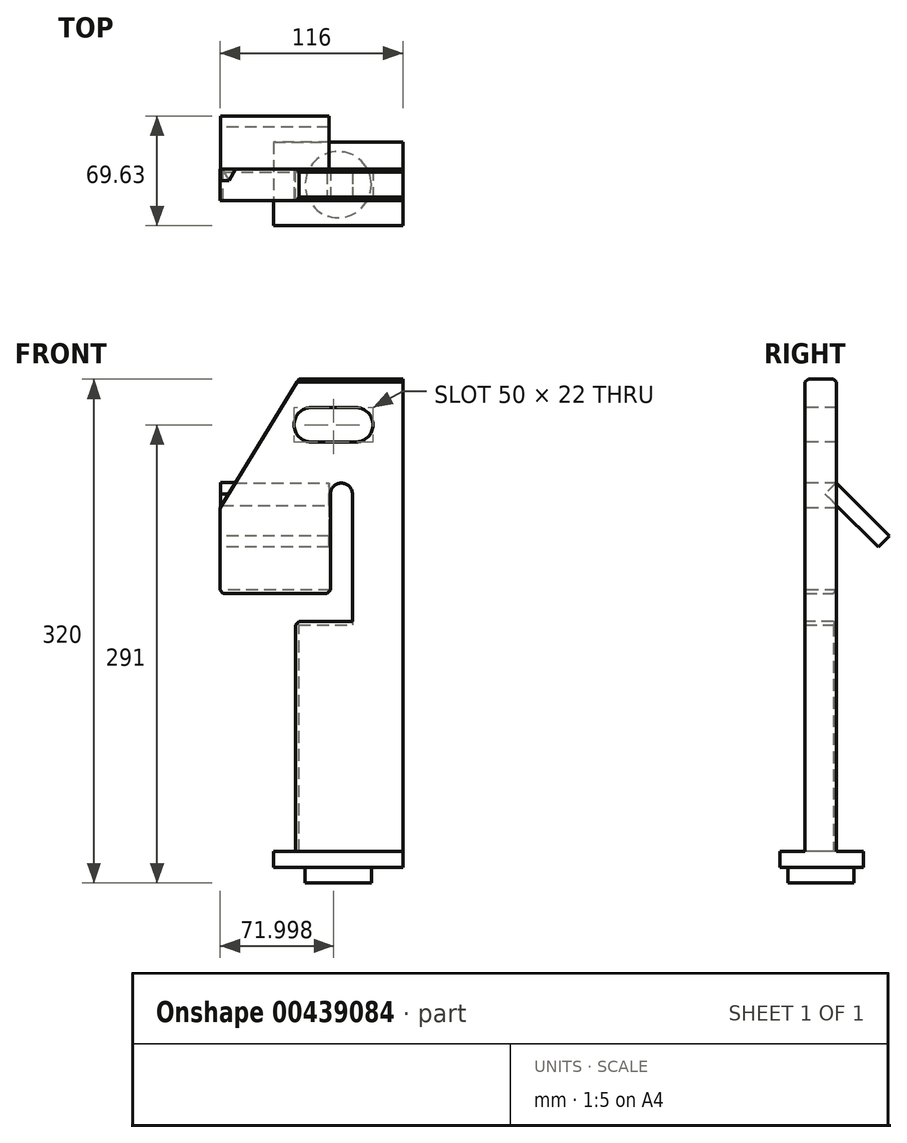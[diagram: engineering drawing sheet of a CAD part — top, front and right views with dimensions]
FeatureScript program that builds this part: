
annotation { "Feature Type Name" : "Feature", "Feature Type Description" : "" }
export const myFeature = defineFeature(function(context is Context, id is Id, definition is map)
    precondition{}
    {
        {
            var Q0;
            Q0=qCreatedBy(makeId("Front.planeOp"),FACE);
            var sketch = newSketch(context, id + "F0", { "sketchPlane" : qUnion([Q0])});
            skLineSegment(sketch, "E0.bottom", {"start": v(-146.6, 260.99) * mm, "end": v(-30.6, 260.99) * mm});
            skLineSegment(sketch, "E0.top", {"start": v(-146.6, -39.01) * mm, "end": v(-30.6, -39.01) * mm});
            skLineSegment(sketch, "E0.left", {"start": v(-146.6, 260.99) * mm, "end": v(-146.6, -39.01) * mm});
            skLineSegment(sketch, "E0.right", {"start": v(-30.6, 260.99) * mm, "end": v(-30.6, -39.01) * mm});
            skLineSegment(sketch, "E1.bottom", {"start": v(-30.6, -39.01) * mm, "end": v(-112.6, -39.01) * mm});
            skLineSegment(sketch, "E1.top", {"start": v(-30.6, -49.01) * mm, "end": v(-112.6, -49.01) * mm});
            skLineSegment(sketch, "E1.left", {"start": v(-30.6, -39.01) * mm, "end": v(-30.6, -49.01) * mm});
            skLineSegment(sketch, "E1.right", {"start": v(-112.6, -39.01) * mm, "end": v(-112.6, -49.01) * mm});
            skLineSegment(sketch, "E2.top", {"start": v(-50.6, -49.01) * mm, "end": v(-92.6, -49.01) * mm});
            skSolve(sketch);
        }
        {
            var Q0;
            Q0 = qSketchRegion(id + "F0", true);
            extrude(context, id + "F1", {"entities" : qUnion([Q0]), "oppositeDirection" : true, "depth" : 20 * mm, "offsetDistance" : 25 * mm});
        }
        {
            var Q0;
            Q0=makeQuery(id+"F1.opExtrude","CAP_FACE",FACE,{"disambiguationData":[OSD([sQuery(id+"F0.wireOp",EDGE,"E0.bottom"),sQuery(id+"F0.wireOp",EDGE,"E0.top"),sQuery(id+"F0.wireOp",EDGE,"E0.left"),sQuery(id+"F0.wireOp",EDGE,"E0.right")])],"isStart":true});
            var sketch = newSketch(context, id + "F2", { "sketchPlane" : qUnion([Q0])});
            skLineSegment(sketch, "E3.bottom", {"start": v(-158.6, -39.01) * mm, "end": v(-98.6, -39.01) * mm});
            skLineSegment(sketch, "E3.top", {"start": v(-158.6, 124.99) * mm, "end": v(-98.6, 124.99) * mm});
            skLineSegment(sketch, "E3.left", {"start": v(-158.6, -39.01) * mm, "end": v(-158.6, 124.99) * mm});
            skLineSegment(sketch, "E3.right", {"start": v(-98.6, -39.01) * mm, "end": v(-98.6, 124.99) * mm});
            skLineSegment(sketch, "E4.bottom", {"start": v(-98.6, 124.99) * mm, "end": v(-62.6, 124.99) * mm});
            skLineSegment(sketch, "E4.top", {"start": v(-98.6, 106.99) * mm, "end": v(-62.6, 106.99) * mm});
            skLineSegment(sketch, "E4.left", {"start": v(-98.6, 124.99) * mm, "end": v(-98.6, 106.99) * mm});
            skLineSegment(sketch, "E4.right", {"start": v(-62.6, 124.99) * mm, "end": v(-62.6, 106.99) * mm});
            skLineSegment(sketch, "E5.bottom", {"start": v(-62.6, 124.99) * mm, "end": v(-76.6, 124.99) * mm});
            skLineSegment(sketch, "E5.top", {"start": v(-62.6, 187.99) * mm, "end": v(-76.6, 187.99) * mm});
            skLineSegment(sketch, "E5.left", {"start": v(-62.6, 124.99) * mm, "end": v(-62.6, 187.99) * mm});
            skLineSegment(sketch, "E5.right", {"start": v(-76.6, 124.99) * mm, "end": v(-76.6, 187.99) * mm});
            skArc(sketch, "E6", {"start": v(-62.6, 187.99) * mm, "mid": v(-69.6, 194.99) * mm, "end": v(-76.6, 187.99) * mm});
            skLineSegment(sketch, "E7", {"start": v(-96.6, 260.99) * mm, "end": v(-146.6, 178.99) * mm});
            skSolve(sketch);
        }
        {
            var Q0;
            Q0 = qSketchRegion(id + "F2", true);
            var Q1;
            {var subQ0=sQuery(id+"F2.wireOp",EDGE,"E7");Q1=makeQuery(id+"F2.imprint","IMPRINT",FACE,{"disambiguationData":[TD([[makeQuery(id+"F2.imprint","IMPRINT",EDGE,{"derivedFrom":subQ0}),-1.0]])]});}
            extrude(context, id + "F3", {"entities" : qUnion([Q0, Q1]), "operationType" : NewBodyOperationType.REMOVE, "oppositeDirection" : true, "depth" : 25 * mm, "offsetDistance" : 25 * mm});
        }
        {
            var Q0;
            Q0=makeQuery(id+"F1.opExtrude","CAP_FACE",FACE,{"disambiguationData":[OSD([sQuery(id+"F0.wireOp",EDGE,"E0.bottom"),sQuery(id+"F0.wireOp",EDGE,"E0.top"),sQuery(id+"F0.wireOp",EDGE,"E0.left"),sQuery(id+"F0.wireOp",EDGE,"E0.right")])],"isStart":true});
            var sketch = newSketch(context, id + "F4", { "sketchPlane" : qUnion([Q0])});
            skLineSegment(sketch, "E8.bottom", {"start": v(-60.6, 242.99) * mm, "end": v(-88.6, 242.99) * mm});
            skLineSegment(sketch, "E8.top", {"start": v(-60.6, 220.99) * mm, "end": v(-88.6, 220.99) * mm});
            skLineSegment(sketch, "E8.left", {"start": v(-60.6, 242.99) * mm, "end": v(-60.6, 220.99) * mm});
            skLineSegment(sketch, "E8.right", {"start": v(-88.6, 242.99) * mm, "end": v(-88.6, 220.99) * mm});
            skArc(sketch, "E9", {"start": v(-60.6, 220.99) * mm, "mid": v(-49.6, 231.99) * mm, "end": v(-60.6, 242.99) * mm});
            skArc(sketch, "E10", {"start": v(-88.6, 242.99) * mm, "mid": v(-99.6, 231.99) * mm, "end": v(-88.6, 220.99) * mm});
            skSolve(sketch);
        }
        {
            var Q0;
            Q0 = qSketchRegion(id + "F4", true);
            extrude(context, id + "F5", {"entities" : qUnion([Q0]), "operationType" : NewBodyOperationType.REMOVE, "oppositeDirection" : true, "depth" : 25 * mm, "offsetDistance" : 25 * mm});
        }
        {
            var Q0;
            Q0=makeQuery(id+"F1.opExtrude","CAP_FACE",FACE,{"disambiguationData":[OSD([sQuery(id+"F0.wireOp",EDGE,"E0.bottom"),sQuery(id+"F0.wireOp",EDGE,"E0.top"),sQuery(id+"F0.wireOp",EDGE,"E0.left"),sQuery(id+"F0.wireOp",EDGE,"E0.right"),sQuery(id+"F0.wireOp",EDGE,"E1.top"),sQuery(id+"F0.wireOp",EDGE,"E1.left"),sQuery(id+"F0.wireOp",EDGE,"E1.right"),sQuery(id+"F0.wireOp",EDGE,"E2.bottom"),sQuery(id+"F0.wireOp",EDGE,"E2.left"),sQuery(id+"F0.wireOp",EDGE,"E2.right")])],"isStart":true});
            var sketch = newSketch(context, id + "F6", { "sketchPlane" : qUnion([Q0])});
            skLineSegment(sketch, "E11", {"start": v(-98.6, -39.01) * mm, "end": v(-30.6, -39.01) * mm});
            skLineSegment(sketch, "E12", {"start": v(-30.6, -49.01) * mm, "end": v(-30.6, -49.01) * mm});
            skSolve(sketch);
        }
        {
            var Q0;
            {var subQ6=sQuery(id+"F6.wireOp",EDGE,"E11");Q0=makeQuery(id+"F6.imprint","IMPRINT",FACE,{"disambiguationData":[TD([[makeQuery(id+"F6.imprint","IMPRINT",EDGE,{"derivedFrom":subQ6}),-1.0]])]});}
            extrude(context, id + "F7", {"entities" : qUnion([Q0]), "operationType" : NewBodyOperationType.ADD, "depth" : 16 * mm, "offsetDistance" : 25 * mm});
        }
        {
            var Q0;
            Q0=makeQuery(id+"F1.opExtrude","CAP_FACE",FACE,{"disambiguationData":[OSD([sQuery(id+"F0.wireOp",EDGE,"E0.bottom"),sQuery(id+"F0.wireOp",EDGE,"E0.top"),sQuery(id+"F0.wireOp",EDGE,"E0.left"),sQuery(id+"F0.wireOp",EDGE,"E0.right"),sQuery(id+"F0.wireOp",EDGE,"E1.top"),sQuery(id+"F0.wireOp",EDGE,"E1.left"),sQuery(id+"F0.wireOp",EDGE,"E1.right"),sQuery(id+"F0.wireOp",EDGE,"E2.bottom"),sQuery(id+"F0.wireOp",EDGE,"E2.left"),sQuery(id+"F0.wireOp",EDGE,"E2.right")])],"isStart":false});
            var sketch = newSketch(context, id + "F8", { "sketchPlane" : qUnion([Q0])});
            skLineSegment(sketch, "E13", {"start": v(98.6, -39.01) * mm, "end": v(30.6, -39.01) * mm});
            skLineSegment(sketch, "E14", {"start": v(30.6, -49.01) * mm, "end": v(30.6, -49.01) * mm});
            skSolve(sketch);
        }
        {
            var Q0;
            {var subQ0=sQuery(id+"F0.wireOp",EDGE,"E2.top");var subQ1=sQuery(id+"F0.wireOp",EDGE,"E1.top");Q0=makeQuery(id+"F10.boolean.opBoolean","MERGE",FACE,{"derivedFrom":[makeQuery(id+"F7.boolean.opBoolean","MERGE",FACE,{"derivedFrom":[makeQuery(id+"F1.opExtrude","SWEPT_FACE",FACE,{"disambiguationData":[OSD([subQ1,subQ0])]}),makeQuery(id+"F7.opExtrude","SWEPT_FACE",FACE,{"disambiguationData":[OSD([subQ1,subQ0])]})]}),makeQuery(id+"F10.opExtrude","SWEPT_FACE",FACE,{"disambiguationData":[OSD([subQ1,subQ0])]})]});}
            var sketch = newSketch(context, id + "F9", { "sketchPlane" : qUnion([Q0])});
            skCircle(sketch, "E15", {"center": v(-71.6, -10) * mm, "radius": 21 * mm});
            skSolve(sketch);
        }
        {
            var Q0;
            {var subQ9=sQuery(id+"F8.wireOp",EDGE,"E13");Q0=makeQuery(id+"F8.imprint","IMPRINT",FACE,{"disambiguationData":[TD([[makeQuery(id+"F8.imprint","IMPRINT",EDGE,{"derivedFrom":subQ9}),1.0]])]});}
            extrude(context, id + "F10", {"entities" : qUnion([Q0]), "operationType" : NewBodyOperationType.ADD, "depth" : 17 * mm, "offsetDistance" : 25 * mm});
        }
        {
            var Q0;
            Q0 = qSketchRegion(id + "F9", true);
            extrude(context, id + "F11", {"entities" : qUnion([Q0]), "operationType" : NewBodyOperationType.ADD, "depth" : 10 * mm, "offsetDistance" : 25 * mm});
        }
        {
            var Q0;
            Q0=makeQuery(id+"F1.opExtrude","CAP_FACE",FACE,{"disambiguationData":[OSD([sQuery(id+"F0.wireOp",EDGE,"E0.bottom"),sQuery(id+"F0.wireOp",EDGE,"E0.top"),sQuery(id+"F0.wireOp",EDGE,"E0.left"),sQuery(id+"F0.wireOp",EDGE,"E0.right"),sQuery(id+"F0.wireOp",EDGE,"E1.top"),sQuery(id+"F0.wireOp",EDGE,"E1.left"),sQuery(id+"F0.wireOp",EDGE,"E1.right"),sQuery(id+"F0.wireOp",EDGE,"E2.top")])],"isStart":false});
            var sketch = newSketch(context, id + "F12", { "sketchPlane" : qUnion([Q0])});
            skLineSegment(sketch, "E16", {"start": v(69.6, 194.99) * mm, "end": v(136.84, 194.99) * mm});
            skSolve(sketch);
        }
        {
            var Q0;
            Q0=makeQuery(id+"F3.boolean.opBoolean","COPY",EDGE,{"derivedFrom":makeQuery(id+"F3.opExtrude","CAP_EDGE",EDGE,{"disambiguationData":[OSD([sQuery(id+"F2.wireOp",EDGE,"E3.right")])],"isStart":true})});
            var Q1;
            Q1=makeQuery(id+"F3.boolean.opBoolean","INTERSECT",EDGE,{"derivedFrom":[makeQuery(id+"F1.opExtrude","CAP_FACE",FACE,{"disambiguationData":[OSD([sQuery(id+"F0.wireOp",EDGE,"E0.bottom"),sQuery(id+"F0.wireOp",EDGE,"E0.top"),sQuery(id+"F0.wireOp",EDGE,"E0.left"),sQuery(id+"F0.wireOp",EDGE,"E0.right"),sQuery(id+"F0.wireOp",EDGE,"E1.top"),sQuery(id+"F0.wireOp",EDGE,"E1.left"),sQuery(id+"F0.wireOp",EDGE,"E1.right"),sQuery(id+"F0.wireOp",EDGE,"E2.bottom"),sQuery(id+"F0.wireOp",EDGE,"E2.left"),sQuery(id+"F0.wireOp",EDGE,"E2.right")])],"isStart":false}),makeQuery(id+"F3.opExtrude","SWEPT_FACE",FACE,{"disambiguationData":[OSD([sQuery(id+"F2.wireOp",EDGE,"E3.right")])]})]});
            chamfer(context, id + "F13", {"entities" : qUnion([Q0, Q1]), "width" : 2 * mm, "tangentPropagation" : true});
        }
        {
            var Q0;
            Q0=makeQuery(id+"F3.boolean.opBoolean","INTERSECT",EDGE,{"derivedFrom":[makeQuery(id+"F1.opExtrude","SWEPT_FACE",FACE,{"disambiguationData":[OSD([sQuery(id+"F0.wireOp",EDGE,"E0.left")])]}),makeQuery(id+"F3.opExtrude","SWEPT_FACE",FACE,{"disambiguationData":[OSD([sQuery(id+"F2.wireOp",EDGE,"E3.top"),sQuery(id+"F2.wireOp",EDGE,"E4.bottom")])]})]});
            var Q1;
            Q1=makeQuery(id+"F3.boolean.opBoolean","COPY",EDGE,{"derivedFrom":makeQuery(id+"F3.opExtrude","SWEPT_EDGE",EDGE,{"disambiguationData":[OSD([sQuery(id+"F2.wireOp",EDGE,"E3.right"),sQuery(id+"F2.wireOp",EDGE,"E4.top"),sQuery(id+"F2.wireOp",EDGE,"E4.left")])]})});
            var Q2;
            Q2=makeQuery(id+"F3.boolean.opBoolean","COPY",EDGE,{"derivedFrom":makeQuery(id+"F3.opExtrude","SWEPT_EDGE",EDGE,{"disambiguationData":[OSD([sQuery(id+"F2.wireOp",EDGE,"E4.bottom"),sQuery(id+"F2.wireOp",EDGE,"E5.bottom"),sQuery(id+"F2.wireOp",EDGE,"E5.right")])]})});
            var Q3;
            Q3=makeQuery(id+"F3.boolean.opBoolean","COPY",EDGE,{"derivedFrom":makeQuery(id+"F3.opExtrude","SWEPT_EDGE",EDGE,{"disambiguationData":[OSD([sQuery(id+"F0.wireOp",EDGE,"E0.bottom"),sQuery(id+"F2.wireOp",EDGE,"E7")])]})});
            chamfer(context, id + "F14", {"entities" : qUnion([Q0, Q1, Q2, Q3]), "width" : 2 * mm, "tangentPropagation" : true});
        }
        {
            var Q0;
            Q0=makeQuery(id+"F3.boolean.opBoolean","COPY",EDGE,{"derivedFrom":makeQuery(id+"F3.opExtrude","CAP_EDGE",EDGE,{"disambiguationData":[OSD([sQuery(id+"F2.wireOp",EDGE,"E3.top"),sQuery(id+"F2.wireOp",EDGE,"E4.bottom")])],"isStart":true})});
            var Q1;
            Q1=makeQuery(id+"F3.boolean.opBoolean","INTERSECT",EDGE,{"derivedFrom":[makeQuery(id+"F1.opExtrude","CAP_FACE",FACE,{"disambiguationData":[OSD([sQuery(id+"F0.wireOp",EDGE,"E0.bottom"),sQuery(id+"F0.wireOp",EDGE,"E0.top"),sQuery(id+"F0.wireOp",EDGE,"E0.left"),sQuery(id+"F0.wireOp",EDGE,"E0.right"),sQuery(id+"F0.wireOp",EDGE,"E1.top"),sQuery(id+"F0.wireOp",EDGE,"E1.left"),sQuery(id+"F0.wireOp",EDGE,"E1.right"),sQuery(id+"F0.wireOp",EDGE,"E2.bottom"),sQuery(id+"F0.wireOp",EDGE,"E2.left"),sQuery(id+"F0.wireOp",EDGE,"E2.right")])],"isStart":false}),makeQuery(id+"F3.opExtrude","SWEPT_FACE",FACE,{"disambiguationData":[OSD([sQuery(id+"F2.wireOp",EDGE,"E3.top"),sQuery(id+"F2.wireOp",EDGE,"E4.bottom")])]})]});
            var Q2;
            Q2=makeQuery(id+"F3.boolean.opBoolean","COPY",EDGE,{"derivedFrom":makeQuery(id+"F3.opExtrude","CAP_EDGE",EDGE,{"disambiguationData":[OSD([sQuery(id+"F2.wireOp",EDGE,"E4.top")])],"isStart":true})});
            var Q3;
            Q3=makeQuery(id+"F3.boolean.opBoolean","INTERSECT",EDGE,{"derivedFrom":[makeQuery(id+"F1.opExtrude","CAP_FACE",FACE,{"disambiguationData":[OSD([sQuery(id+"F0.wireOp",EDGE,"E0.bottom"),sQuery(id+"F0.wireOp",EDGE,"E0.top"),sQuery(id+"F0.wireOp",EDGE,"E0.left"),sQuery(id+"F0.wireOp",EDGE,"E0.right"),sQuery(id+"F0.wireOp",EDGE,"E1.top"),sQuery(id+"F0.wireOp",EDGE,"E1.left"),sQuery(id+"F0.wireOp",EDGE,"E1.right"),sQuery(id+"F0.wireOp",EDGE,"E2.bottom"),sQuery(id+"F0.wireOp",EDGE,"E2.left"),sQuery(id+"F0.wireOp",EDGE,"E2.right")])],"isStart":false}),makeQuery(id+"F3.opExtrude","SWEPT_FACE",FACE,{"disambiguationData":[OSD([sQuery(id+"F2.wireOp",EDGE,"E4.top")])]})]});
            var Q4;
            Q4=makeQuery(id+"F1.opExtrude","CAP_EDGE",EDGE,{"disambiguationData":[OSD([sQuery(id+"F0.wireOp",EDGE,"E0.bottom")])],"isStart":true});
            var Q5;
            Q5=makeQuery(id+"F1.opExtrude","CAP_EDGE",EDGE,{"disambiguationData":[OSD([sQuery(id+"F0.wireOp",EDGE,"E0.bottom")])],"isStart":false});
            chamfer(context, id + "F15", {"entities" : qUnion([Q0, Q1, Q2, Q3, Q4, Q5]), "width" : 2 * mm, "tangentPropagation" : true});
        }
        {
            var Q0;
            Q0=makeQuery(id+"F1.opExtrude","CAP_FACE",FACE,{"disambiguationData":[OSD([sQuery(id+"F0.wireOp",EDGE,"E0.bottom"),sQuery(id+"F0.wireOp",EDGE,"E0.top"),sQuery(id+"F0.wireOp",EDGE,"E0.left"),sQuery(id+"F0.wireOp",EDGE,"E0.right"),sQuery(id+"F0.wireOp",EDGE,"E1.top"),sQuery(id+"F0.wireOp",EDGE,"E1.left"),sQuery(id+"F0.wireOp",EDGE,"E1.right"),sQuery(id+"F0.wireOp",EDGE,"E2.top")])],"isStart":false});
            var Q1;
            Q1=sQuery(id+"F12.wireOp",EDGE,"E16");
            cPlane(context, id + "F16", {"entities" : qUnion([Q0, Q1]), "cplaneType" : CPlaneType.LINE_ANGLE, "offset" : 25 * mm, "angle" : 45 * degree, "width" : 150 * mm, "height" : 150 * mm});
        }
        {
            var Q0;
            {var subQ11=sQuery(id+"F12.wireOp",EDGE,"E16");Q0=makeQuery(id+"F12.imprint","IMPRINT",FACE,{"disambiguationData":[TD([[makeQuery(id+"F12.imprint","IMPRINT",EDGE,{"derivedFrom":subQ11}),1.0]])]});}
            var Q1;
            Q1=sQuery(id+"F12.wireOp",EDGE,"E16");
            cPlane(context, id + "F17", {"entities" : qUnion([Q0, Q1]), "cplaneType" : CPlaneType.LINE_ANGLE, "offset" : 25 * mm, "angle" : 45 * degree, "oppositeDirection" : true, "width" : 150 * mm, "height" : 150 * mm});
        }
        {
            var Q0;
            Q0=qCreatedBy(id+"F17.planeOp",FACE);
            var sketch = newSketch(context, id + "F18", { "sketchPlane" : qUnion([Q0])});
            skLineSegment(sketch, "E17.bottom", {"start": v(-77.41, 124.07) * mm, "end": v(-146.22, 124.07) * mm});
            skLineSegment(sketch, "E17.top", {"start": v(-77.41, 76.18) * mm, "end": v(-146.22, 76.18) * mm});
            skLineSegment(sketch, "E17.left", {"start": v(-77.41, 124.07) * mm, "end": v(-77.41, 76.18) * mm});
            skLineSegment(sketch, "E17.right", {"start": v(-146.22, 124.07) * mm, "end": v(-146.22, 76.18) * mm});
            skSolve(sketch);
        }
        {
            var Q0;
            Q0 = qSketchRegion(id + "F18", true);
            extrude(context, id + "F19", {"entities" : qUnion([Q0]), "operationType" : NewBodyOperationType.ADD, "depth" : 10 * mm, "offsetDistance" : 25 * mm});
        }
    });
